# Revit family: Plumbing_Pipes_Aignep_Flexible-Hose-Connected-90806
name_source: partatom
category: Pipe Accessories
revit_build: Autodesk Revit 2018 (Build: 20170223_1515(x64)
units: mm (PartAtom-declared; Revit-internal decimal feet)

## family parameters
Cut with Voids When Loaded = No
OmniClass Number = 23.27.43.00
OmniClass Title = Pipe Fittings
Part Type = Normal
Round Connector Dimension = Use Diameter
Shared = No

## types (1)
- 90806
    Article Code = 90806
    Assembly Code = D2040100
    BIMobject category = Pipes
    Description = Flexible hose connected
    Design country = Italy
    Edition number = 1
    IFC Classification = Pipe Fitting
    Keynote = 15410
    Manufacturer = Aignep Spa
    Manufacturer country = Italy
    Manufacturer name = Aignep Spa
    Material main = Plastic
    Model = 90806
    OmniClass Code = 23-27 43 00
    OmniClass Description = Pipe Fittings
    Product Guid = ca6625da-5f0e-4c1a-bc28-d38577bcd021
    Product Material = AIGNEP - Aluminium - Grey
    Product SKU = Flexible-Hose-Connected-90806
    Product certification = https://www.aignep.com
    Product data url = https://www.bimobject.com
    Product family = INFINITY
    Product group = Tubes
    Product name = Flexible Hose Connected - 90806
    Product url = https://www.aignep.com
    QR code = https://www.bimobject.com
    URL = https://www.aignep.com

## geometry (parser evidence)
native form markers: Sweep x1
no freeform markers — native parametric forms only
